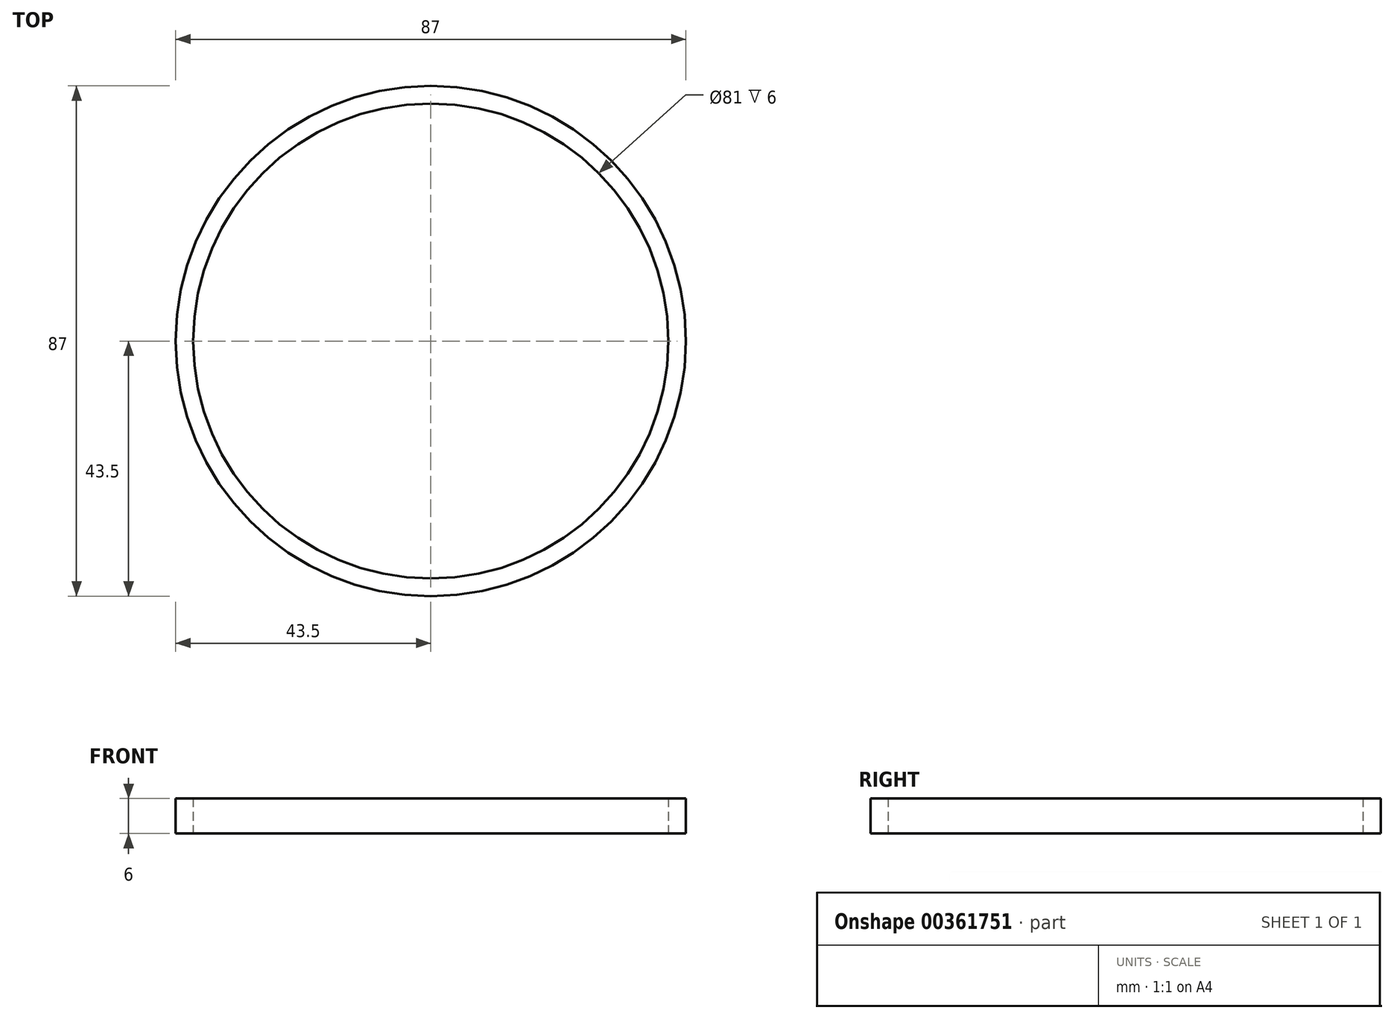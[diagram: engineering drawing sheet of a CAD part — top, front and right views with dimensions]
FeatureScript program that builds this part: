
annotation { "Feature Type Name" : "Feature", "Feature Type Description" : "" }
export const myFeature = defineFeature(function(context is Context, id is Id, definition is map)
    precondition{}
    {
        {
            var Q0;
            Q0=qCreatedBy(makeId("Top.planeOp"),FACE);
            var sketch = newSketch(context, id + "F0", { "sketchPlane" : qUnion([Q0])});
            skCircle(sketch, "E0", {"center": v(0, 0) * mm, "radius": 40.5 * mm});
            skCircle(sketch, "E1.0", {"center": v(0, 0) * mm, "radius": 43.5 * mm});
            skCircle(sketch, "E2", {"center": v(0, 0) * mm, "radius": 2.25 * mm});
            skCircle(sketch, "E3.1.0.0", {"center": v(8, 0) * mm, "radius": 2.25 * mm});
            skCircle(sketch, "E3.2.0.0", {"center": v(16, 0) * mm, "radius": 2.25 * mm});
            skCircle(sketch, "E3.3.0.0", {"center": v(24, 0) * mm, "radius": 2.25 * mm});
            skCircle(sketch, "E3.4.0.0", {"center": v(32, 0) * mm, "radius": 2.25 * mm});
            skLineSegment(sketch, "E3.direction1", {"start": v(0, 0) * mm, "end": v(8, 0) * mm, "construction": true});
            skCircle(sketch, "E4.0.1.0", {"center": v(0, 8) * mm, "radius": 2.25 * mm});
            skCircle(sketch, "E4.0.1.1", {"center": v(8, 8) * mm, "radius": 2.25 * mm});
            skCircle(sketch, "E4.0.1.2", {"center": v(16, 8) * mm, "radius": 2.25 * mm});
            skCircle(sketch, "E4.0.1.3", {"center": v(24, 8) * mm, "radius": 2.25 * mm});
            skCircle(sketch, "E4.0.1.5", {"center": v(32, 8) * mm, "radius": 2.25 * mm});
            skCircle(sketch, "E4.0.2.0", {"center": v(0, 16) * mm, "radius": 2.25 * mm});
            skCircle(sketch, "E4.0.2.1", {"center": v(8, 16) * mm, "radius": 2.25 * mm});
            skCircle(sketch, "E4.0.2.2", {"center": v(16, 16) * mm, "radius": 2.25 * mm});
            skCircle(sketch, "E4.0.2.3", {"center": v(24, 16) * mm, "radius": 2.25 * mm});
            skCircle(sketch, "E4.0.2.5", {"center": v(32, 16) * mm, "radius": 2.25 * mm});
            skCircle(sketch, "E4.0.3.0", {"center": v(0, 24) * mm, "radius": 2.25 * mm});
            skCircle(sketch, "E4.0.3.1", {"center": v(8, 24) * mm, "radius": 2.25 * mm});
            skCircle(sketch, "E4.0.3.2", {"center": v(16, 24) * mm, "radius": 2.25 * mm});
            skCircle(sketch, "E4.0.3.3", {"center": v(24, 24) * mm, "radius": 2.25 * mm});
            skCircle(sketch, "E4.0.4.0", {"center": v(0, 32) * mm, "radius": 2.25 * mm});
            skCircle(sketch, "E4.0.4.1", {"center": v(8, 32) * mm, "radius": 2.25 * mm});
            skCircle(sketch, "E4.0.4.2", {"center": v(16, 32) * mm, "radius": 2.25 * mm});
            skLineSegment(sketch, "E4.direction1", {"start": v(0, 0) * mm, "end": v(-25, 0) * mm, "construction": true});
            skLineSegment(sketch, "E4.direction2", {"start": v(0, 0) * mm, "end": v(0, 8) * mm, "construction": true});
            skLineSegment(sketch, "E5", {"start": v(0, 0) * mm, "end": v(40, 0) * mm});
            skCircle(sketch, "E6.MirrorC", {"center": v(16, -16) * mm, "radius": 2.25 * mm});
            skCircle(sketch, "E7.MirrorC", {"center": v(24, -16) * mm, "radius": 2.25 * mm});
            skCircle(sketch, "E8.MirrorC", {"center": v(24, -8) * mm, "radius": 2.25 * mm});
            skCircle(sketch, "E9.MirrorC", {"center": v(32, -8) * mm, "radius": 2.25 * mm});
            skCircle(sketch, "E10.MirrorC", {"center": v(0, -8) * mm, "radius": 2.25 * mm});
            skCircle(sketch, "E11.MirrorC", {"center": v(8, -8) * mm, "radius": 2.25 * mm});
            skCircle(sketch, "E12.MirrorC", {"center": v(16, -8) * mm, "radius": 2.25 * mm});
            skCircle(sketch, "E13.MirrorC", {"center": v(8, -24) * mm, "radius": 2.25 * mm});
            skCircle(sketch, "E14.MirrorC", {"center": v(8, -32) * mm, "radius": 2.25 * mm});
            skCircle(sketch, "E15.MirrorC", {"center": v(0, -16) * mm, "radius": 2.25 * mm});
            skCircle(sketch, "E16.MirrorC", {"center": v(16, -24) * mm, "radius": 2.25 * mm});
            skCircle(sketch, "E17.MirrorC", {"center": v(0, -24) * mm, "radius": 2.25 * mm});
            skCircle(sketch, "E18.MirrorC", {"center": v(0, -32) * mm, "radius": 2.25 * mm});
            skCircle(sketch, "E19.MirrorC", {"center": v(16, -32) * mm, "radius": 2.25 * mm});
            skCircle(sketch, "E20.MirrorC", {"center": v(8, -16) * mm, "radius": 2.25 * mm});
            skCircle(sketch, "E21.MirrorC", {"center": v(24, -24) * mm, "radius": 2.25 * mm});
            skCircle(sketch, "E22.MirrorC", {"center": v(32, -16) * mm, "radius": 2.25 * mm});
            skLineSegment(sketch, "E23", {"start": v(0, 40) * mm, "end": v(0, -40) * mm});
            skCircle(sketch, "E24.MirrorC", {"center": v(-8, -8) * mm, "radius": 2.25 * mm});
            skCircle(sketch, "E25.MirrorC", {"center": v(-8, 32) * mm, "radius": 2.25 * mm});
            skCircle(sketch, "E26.MirrorC", {"center": v(-16, -16) * mm, "radius": 2.25 * mm});
            skCircle(sketch, "E27.MirrorC", {"center": v(-32, 16) * mm, "radius": 2.25 * mm});
            skCircle(sketch, "E28.MirrorC", {"center": v(-8, -16) * mm, "radius": 2.25 * mm});
            skCircle(sketch, "E29.MirrorC", {"center": v(-16, -24) * mm, "radius": 2.25 * mm});
            skCircle(sketch, "E30.MirrorC", {"center": v(-24, -16) * mm, "radius": 2.25 * mm});
            skCircle(sketch, "E31.MirrorC", {"center": v(-16, -8) * mm, "radius": 2.25 * mm});
            skCircle(sketch, "E32.MirrorC", {"center": v(-16, 16) * mm, "radius": 2.25 * mm});
            skCircle(sketch, "E33.MirrorC", {"center": v(-24, 24) * mm, "radius": 2.25 * mm});
            skCircle(sketch, "E34.MirrorC", {"center": v(-16, 32) * mm, "radius": 2.25 * mm});
            skCircle(sketch, "E35.MirrorC", {"center": v(-24, 0) * mm, "radius": 2.25 * mm});
            skCircle(sketch, "E36.MirrorC", {"center": v(-32, 0) * mm, "radius": 2.25 * mm});
            skCircle(sketch, "E37.MirrorC", {"center": v(-24, -24) * mm, "radius": 2.25 * mm});
            skCircle(sketch, "E38.MirrorC", {"center": v(-8, 8) * mm, "radius": 2.25 * mm});
            skCircle(sketch, "E39.MirrorC", {"center": v(-16, 8) * mm, "radius": 2.25 * mm});
            skCircle(sketch, "E40.MirrorC", {"center": v(-8, 24) * mm, "radius": 2.25 * mm});
            skCircle(sketch, "E41.MirrorC", {"center": v(-24, -8) * mm, "radius": 2.25 * mm});
            skCircle(sketch, "E42.MirrorC", {"center": v(-24, 8) * mm, "radius": 2.25 * mm});
            skCircle(sketch, "E43.MirrorC", {"center": v(-32, 8) * mm, "radius": 2.25 * mm});
            skCircle(sketch, "E44.MirrorC", {"center": v(-8, -24) * mm, "radius": 2.25 * mm});
            skCircle(sketch, "E45.MirrorC", {"center": v(-16, 24) * mm, "radius": 2.25 * mm});
            skCircle(sketch, "E46.MirrorC", {"center": v(-32, -16) * mm, "radius": 2.25 * mm});
            skCircle(sketch, "E47.MirrorC", {"center": v(-8, 16) * mm, "radius": 2.25 * mm});
            skCircle(sketch, "E48.MirrorC", {"center": v(-32, -8) * mm, "radius": 2.25 * mm});
            skCircle(sketch, "E49.MirrorC", {"center": v(-24, 16) * mm, "radius": 2.25 * mm});
            skCircle(sketch, "E50.MirrorC", {"center": v(-16, -32) * mm, "radius": 2.25 * mm});
            skCircle(sketch, "E51.MirrorC", {"center": v(-16, 0) * mm, "radius": 2.25 * mm});
            skCircle(sketch, "E52.MirrorC", {"center": v(-8, 0) * mm, "radius": 2.25 * mm});
            skCircle(sketch, "E53.MirrorC", {"center": v(-8, -32) * mm, "radius": 2.25 * mm});
            skSolve(sketch);
        }
        {
            var Q0;
            Q0=makeQuery(id+"F0.imprint","IMPRINT",FACE,{"disambiguationData":[TD([[makeQuery(id+"F0.imprint","IMPRINT",EDGE,{"derivedFrom":sQuery(id+"F0.wireOp",EDGE,"E0")}),-1.0]])]});
            extrude(context, id + "F1", {"entities" : qUnion([Q0]), "depth" : 3 * mm, "offsetDistance" : 25 * mm});
        }
        {
            var Q0;
            Q0=makeQuery(id+"F0.imprint","IMPRINT",FACE,{"disambiguationData":[TD([[makeQuery(id+"F0.imprint","IMPRINT",EDGE,{"derivedFrom":sQuery(id+"F0.wireOp",EDGE,"E1.0")}),1.0]])]});
            extrude(context, id + "F2", {"entities" : qUnion([Q0]), "operationType" : NewBodyOperationType.ADD, "depth" : 6 * mm, "offsetDistance" : 25 * mm});
        }
    });
